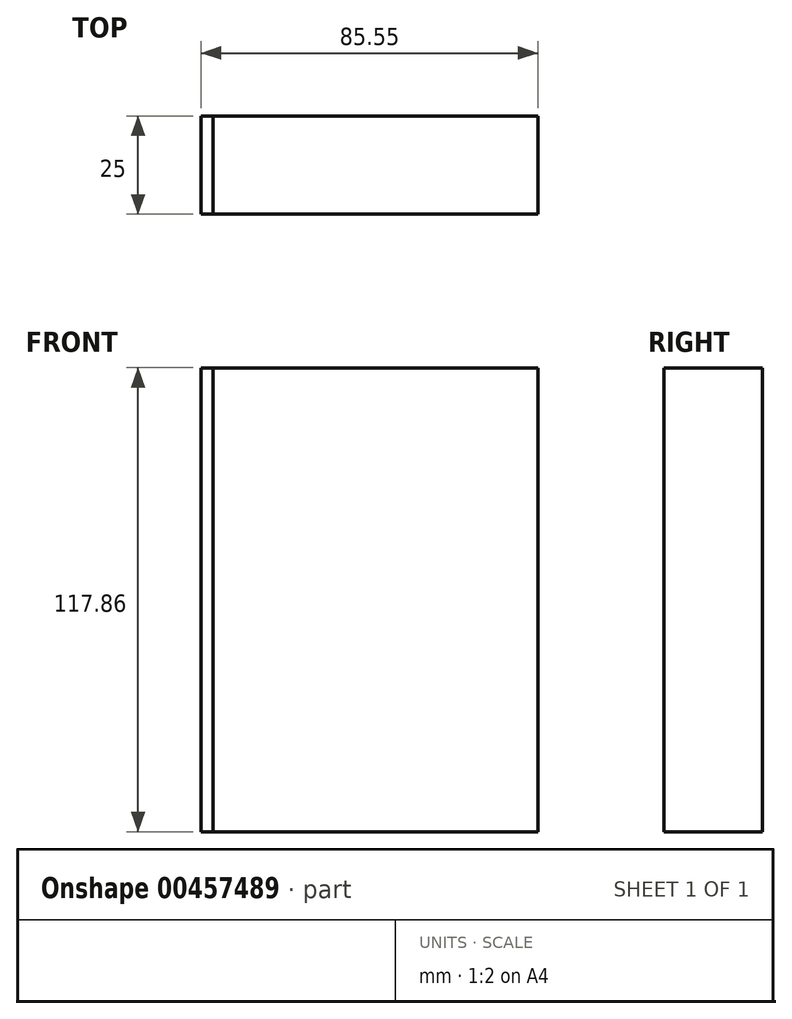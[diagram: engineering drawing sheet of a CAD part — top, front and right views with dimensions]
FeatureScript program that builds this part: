
annotation { "Feature Type Name" : "Feature", "Feature Type Description" : "" }
export const myFeature = defineFeature(function(context is Context, id is Id, definition is map)
    precondition{}
    {
        {
            var Q0;
            Q0=qCreatedBy(makeId("Front.planeOp"),FACE);
            var sketch = newSketch(context, id + "F0", { "sketchPlane" : qUnion([Q0])});
            skLineSegment(sketch, "E0.bottom", {"start": v(-39.44, 47.7) * mm, "end": v(43.1, 47.7) * mm});
            skLineSegment(sketch, "E0.top", {"start": v(-39.44, -55.03) * mm, "end": v(43.1, -55.03) * mm});
            skLineSegment(sketch, "E0.left", {"start": v(-39.44, 47.7) * mm, "end": v(-39.44, -55.03) * mm});
            skLineSegment(sketch, "E0.right", {"start": v(43.1, 47.7) * mm, "end": v(43.1, -55.03) * mm});
            skLineSegment(sketch, "E1.bottom", {"start": v(43.1, 47.7) * mm, "end": v(-39.44, 47.7) * mm});
            skLineSegment(sketch, "E1.top", {"start": v(43.1, 62.83) * mm, "end": v(-39.44, 62.83) * mm});
            skLineSegment(sketch, "E1.left", {"start": v(43.1, 47.7) * mm, "end": v(43.1, 62.83) * mm});
            skLineSegment(sketch, "E1.right", {"start": v(-39.44, 47.7) * mm, "end": v(-39.44, 62.83) * mm});
            skSolve(sketch);
        }
        {
            var Q0;
            Q0 = qSketchRegion(id + "F0", true);
            extrude(context, id + "F1", {"entities" : qUnion([Q0]), "depth" : 25 * mm});
        }
        {
            var Q0;
            Q0=makeQuery(id+"F1.opExtrude","SWEPT_FACE",FACE,{"disambiguationData":[OSD([sQuery(id+"F0.wireOp",EDGE,"E0.left"),sQuery(id+"F0.wireOp",EDGE,"E1.right")])]});
            extrude(context, id + "F2", {"entities" : qUnion([Q0]), "depth" : 3 * mm});
        }
    });
